# Revit family: Sanitary_Installation-Systems_Hansgrohe_iBox-universal-2-Basic-set-with-pre-moun__555
name_source: partatom
category: Plumbing Fixtures
revit_build: Autodesk Revit 2018 (Build: 20170223_1515(x64)
units: mm (PartAtom-declared; Revit-internal decimal feet)

## family parameters
Always vertical = No
Cut with Voids When Loaded = No
OmniClass Number = 23.27.31.29.11
OmniClass Title = Manual Mixing Valves
Part Type = Normal
Room Calculation Point = No
Round Connector Dimension = Use Diameter
Shared = No
Work Plane-Based = Yes

## types (1)
- iBox universal 2 Basic set with pre-mounted angle connection G1/2
    Always visible = Yes
    Connector Description = Water conector 12.7mm
    Date Updated = 2023/11/24
    Default Elevation = 1219.2 mm  [stored 4 ft]
    Description = iBox universal 2 Basic set with pre-mounted angle connection G1/2
    Diameter = 12.7 mm  [stored 0.0416667 ft]
    Manufacturer = Hansgrohe
    Material 1 = Hansgrohe - Metal - Brass
    Material 2 = Hansgrohe - Plastic - Black
    Material 3 = Hansgrohe - Plastic - Light Green
    Material 4 = Hansgrohe - Plastic - Green
    Model = 01510XXX
    Product data url = https://bimobject.com
    Product url = https://pro.hansgrohe.com
    URL = https://www.hansgrohe.com
    Version = 2

note: [stored X ft] marks values corroborated as IEEE doubles in the binary element streams (Revit-internal decimal feet)

## geometry (parser evidence)
native form markers: Sweep x1
no freeform markers — native parametric forms only
